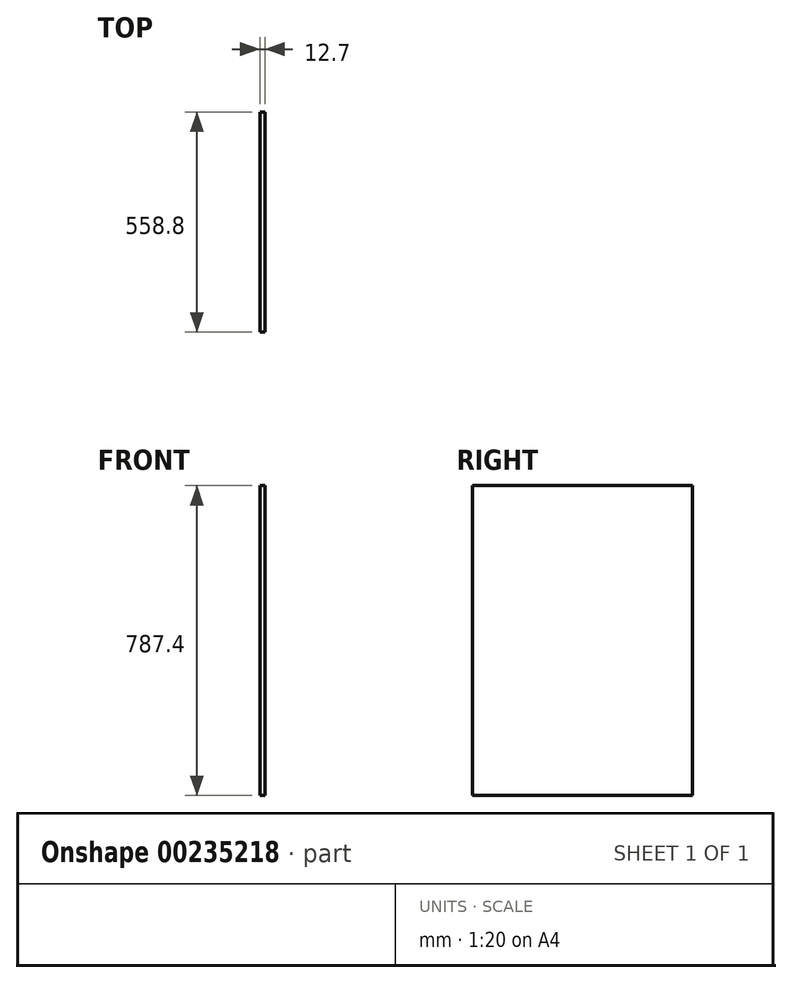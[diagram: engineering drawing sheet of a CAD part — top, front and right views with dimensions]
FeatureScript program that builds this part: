
annotation { "Feature Type Name" : "Feature", "Feature Type Description" : "" }
export const myFeature = defineFeature(function(context is Context, id is Id, definition is map)
    precondition{}
    {
        {
            var Q0;
            Q0=qCreatedBy(makeId("Right.planeOp"),FACE);
            var sketch = newSketch(context, id + "F0", { "sketchPlane" : qUnion([Q0])});
            skLineSegment(sketch, "E0.bottom", {"start": v(-279.4, 393.7) * mm, "end": v(279.4, 393.7) * mm});
            skLineSegment(sketch, "E0.top", {"start": v(-279.4, -393.7) * mm, "end": v(279.4, -393.7) * mm});
            skLineSegment(sketch, "E0.left", {"start": v(-279.4, 393.7) * mm, "end": v(-279.4, -393.7) * mm});
            skLineSegment(sketch, "E0.right", {"start": v(279.4, 393.7) * mm, "end": v(279.4, -393.7) * mm});
            skSolve(sketch);
        }
        {
            var Q0;
            Q0=makeQuery(id+"F0.imprint","IMPRINT",FACE,{"disambiguationData":[TD([[makeQuery(id+"F0.imprint","IMPRINT",EDGE,{"derivedFrom":sQuery(id+"F0.wireOp",EDGE,"E0.bottom")}),-1.0]])]});
            extrude(context, id + "F1", {"entities" : qUnion([Q0]), "depth" : 12.7 * mm});
        }
    });
